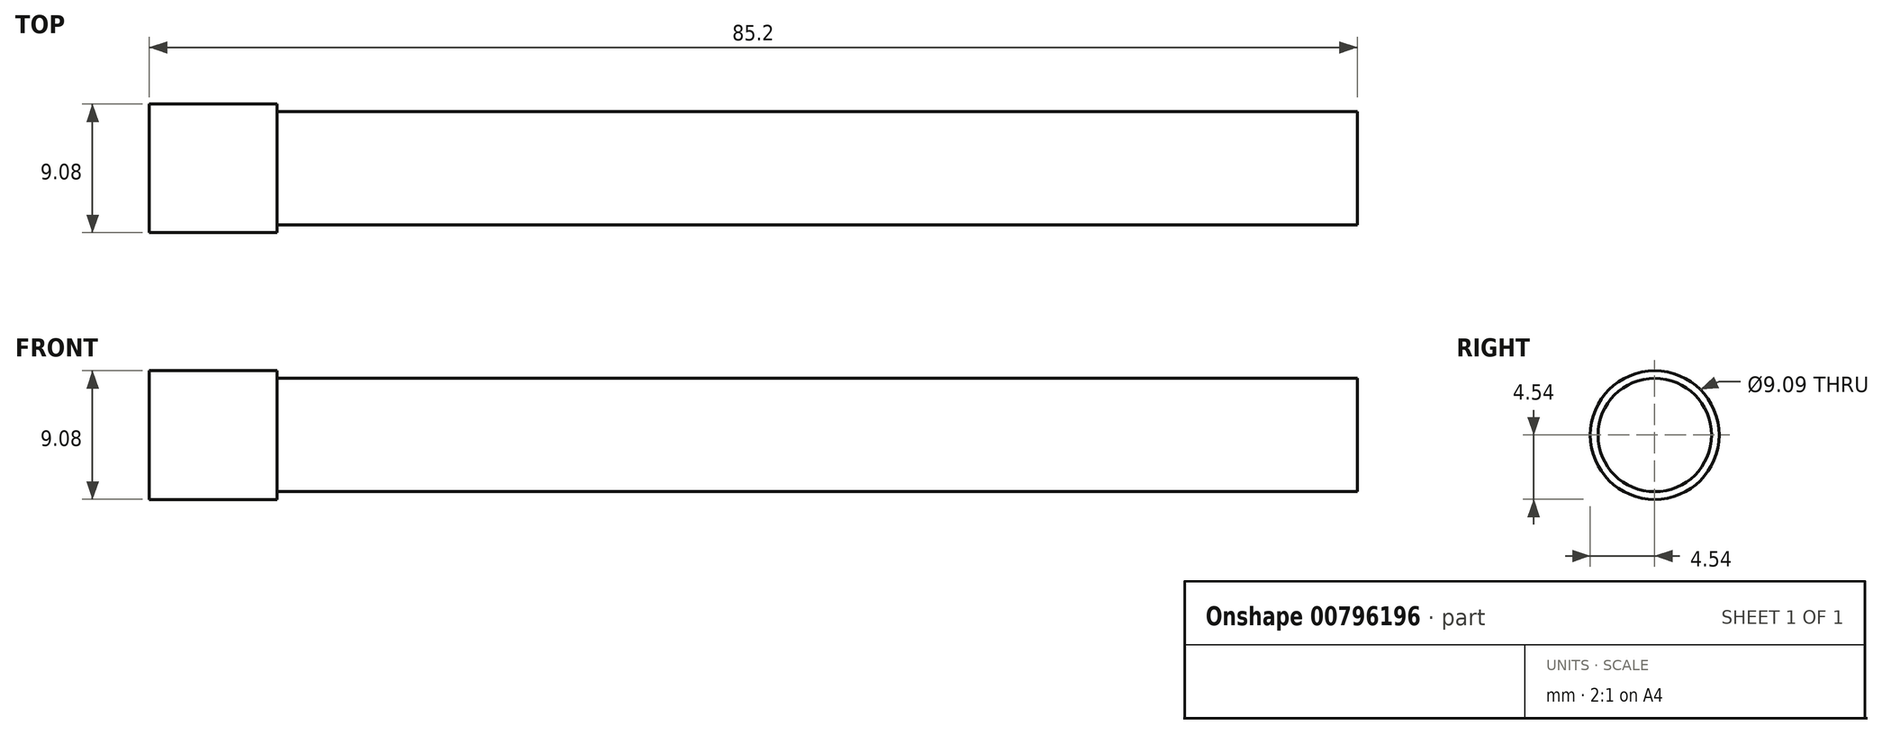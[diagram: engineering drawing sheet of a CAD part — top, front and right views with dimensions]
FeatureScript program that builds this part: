
annotation { "Feature Type Name" : "Feature", "Feature Type Description" : "" }
export const myFeature = defineFeature(function(context is Context, id is Id, definition is map)
    precondition{}
    {
        {
            var Q0;
            Q0=qCreatedBy(makeId("Right.planeOp"),FACE);
            var sketch = newSketch(context, id + "F0", { "sketchPlane" : qUnion([Q0])});
            skCircle(sketch, "E0", {"center": v(0, 0) * mm, "radius": 4 * mm});
            skSolve(sketch);
        }
        {
            var Q0;
            Q0=sQuery(id+"F0.wireOp",EDGE,"E0");
            extrude(context, id + "F1", {"bodyType" : ToolBodyType.SURFACE, "surfaceEntities" : qUnion([Q0]), "depth" : 76.2 * mm, "offsetDistance" : 25 * mm});
        }
        {
            var Q0;
            Q0=qCreatedBy(makeId("Right.planeOp"),FACE);
            var sketch = newSketch(context, id + "F2", { "sketchPlane" : qUnion([Q0])});
            skCircle(sketch, "E1", {"center": v(0, 0) * mm, "radius": 4.54 * mm});
            skSolve(sketch);
        }
        {
            var Q0;
            Q0=sQuery(id+"F2.wireOp",EDGE,"E1");
            extrude(context, id + "F3", {"bodyType" : ToolBodyType.SURFACE, "surfaceEntities" : qUnion([Q0]), "oppositeDirection" : true, "depth" : 9 * mm, "offsetDistance" : 25 * mm});
        }
    });
